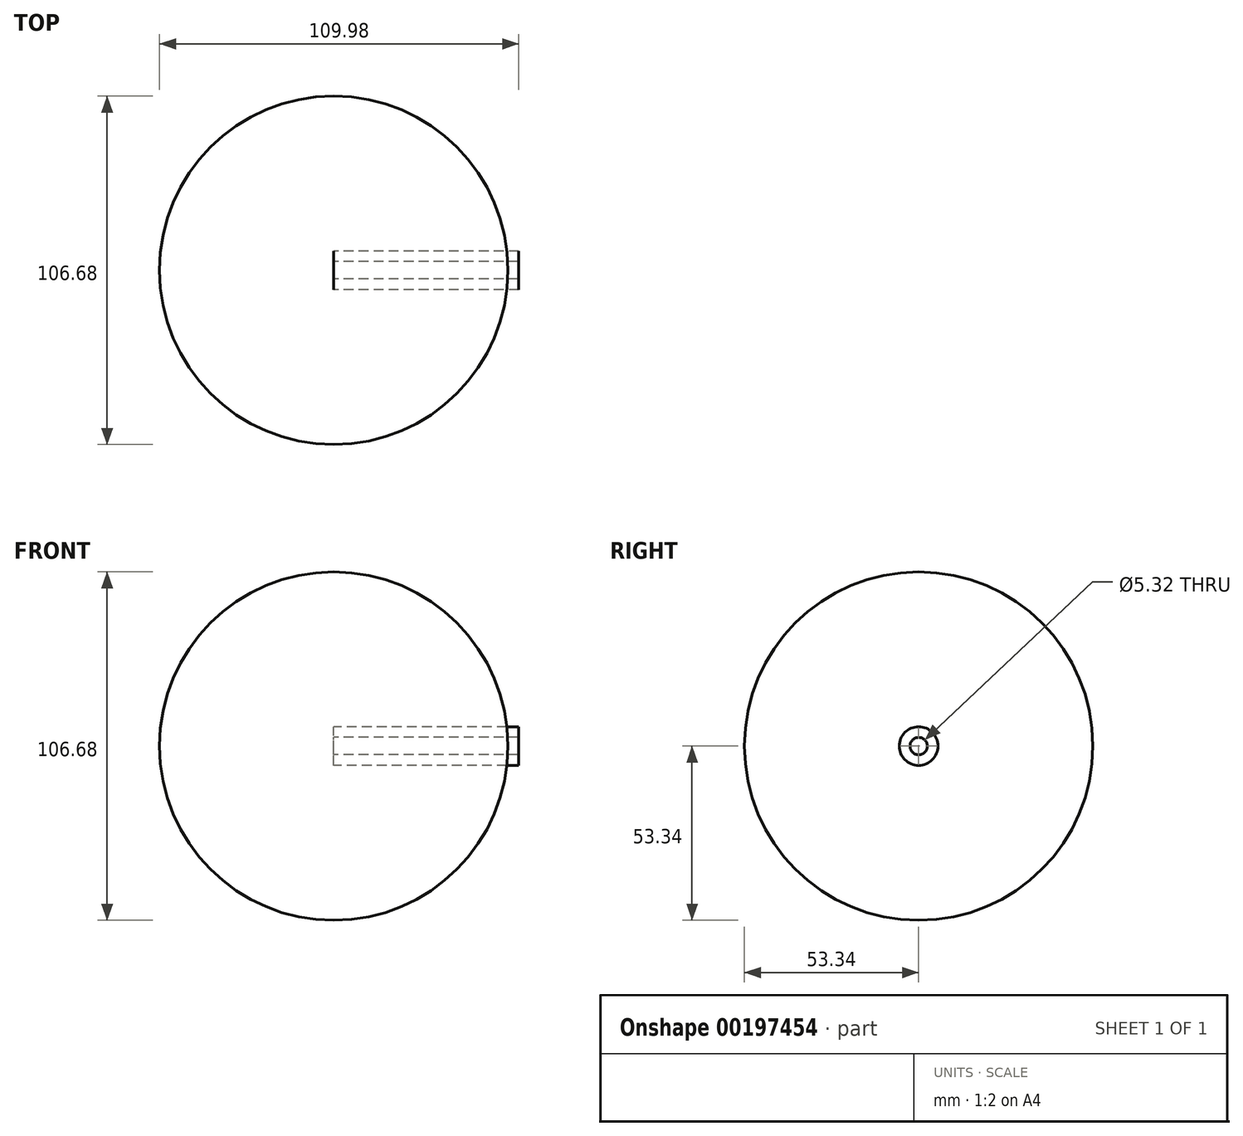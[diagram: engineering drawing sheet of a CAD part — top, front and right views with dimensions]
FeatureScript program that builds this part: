
annotation { "Feature Type Name" : "Feature", "Feature Type Description" : "" }
export const myFeature = defineFeature(function(context is Context, id is Id, definition is map)
    precondition{}
    {
        {
            var Q0;
            Q0=qCreatedBy(makeId("Right.planeOp"),FACE);
            var sketch = newSketch(context, id + "F0", { "sketchPlane" : qUnion([Q0])});
            skArc(sketch, "E0", {"start": v(53.34, 0) * mm, "mid": v(0, 53.34) * mm, "end": v(-53.34, 0) * mm});
            skLineSegment(sketch, "E1", {"start": v(-53.34, 0) * mm, "end": v(53.34, 0) * mm});
            skSolve(sketch);
        }
        {
            var Q0;
            Q0 = qSketchRegion(id + "F0", true);
            var Q1;
            Q1=sQuery(id+"F0.wireOp",EDGE,"E1");
            revolve(context, id + "F1", {"entities" : qUnion([Q0]), "axis" : qUnion([Q1]), "revolveType" : RevolveType.FULL});
        }
        {
            var Q0;
            Q0=qCreatedBy(makeId("Right.planeOp"),FACE);
            var sketch = newSketch(context, id + "F2", { "sketchPlane" : qUnion([Q0])});
            skCircle(sketch, "E2", {"center": v(0, 0) * mm, "radius": 2.66 * mm});
            skCircle(sketch, "E3", {"center": v(0, 0) * mm, "radius": 5.91 * mm});
            skPoint(sketch, "E4.0.midPoint", {"position": v(23.28, -39.87) * mm});
            skSolve(sketch);
        }
        {
            var Q0;
            Q0 = qSketchRegion(id + "F2", true);
            extrude(context, id + "F3", {"entities" : qUnion([Q0]), "depth" : 56.64 * mm});
        }
    });
